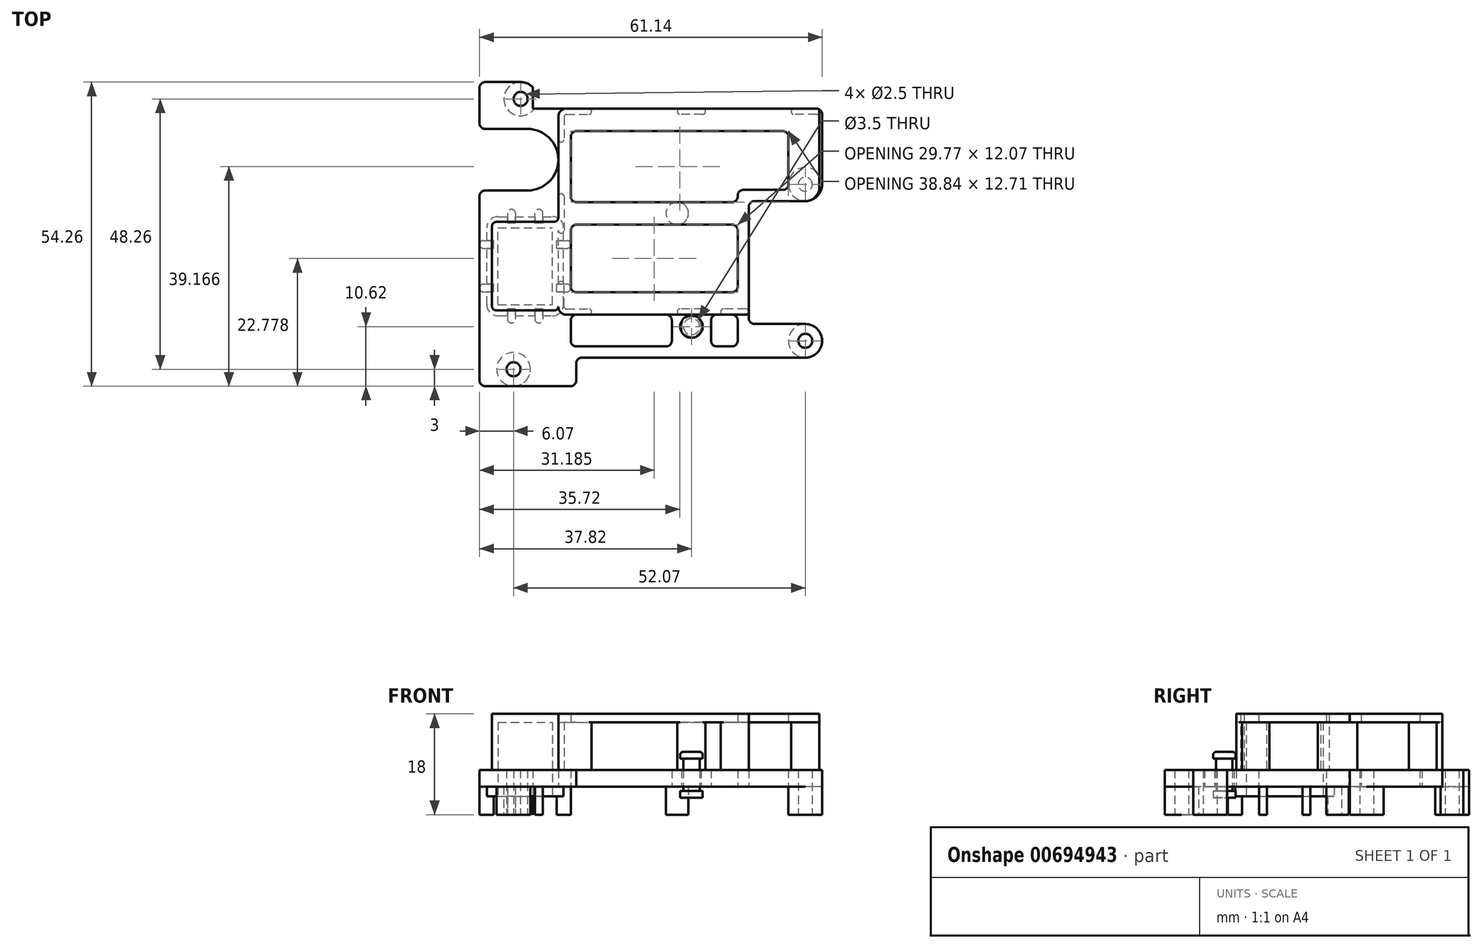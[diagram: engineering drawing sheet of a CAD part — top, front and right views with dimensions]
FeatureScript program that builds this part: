
annotation { "Feature Type Name" : "Feature", "Feature Type Description" : "" }
export const myFeature = defineFeature(function(context is Context, id is Id, definition is map)
    precondition{}
    {
        {
            var Q0;
            Q0=qCreatedBy(makeId("Top.planeOp"),FACE);
            var sketch = newSketch(context, id + "F0", { "sketchPlane" : qUnion([Q0])});
            skCircle(sketch, "E0", {"center": v(0, 0) * mm, "radius": 1.25 * mm});
            skCircle(sketch, "E1", {"center": v(0, 0) * mm, "radius": 3 * mm});
            skCircle(sketch, "E2", {"center": v(1.27, 48.26) * mm, "radius": 2.2 * mm});
            skCircle(sketch, "E3", {"center": v(1.27, 48.26) * mm, "radius": 1.25 * mm});
            skCircle(sketch, "E4", {"center": v(52.07, 33.02) * mm, "radius": 3 * mm});
            skCircle(sketch, "E5", {"center": v(52.07, 33.02) * mm, "radius": 1.25 * mm});
            skCircle(sketch, "E6", {"center": v(52.07, 5.08) * mm, "radius": 3 * mm});
            skCircle(sketch, "E7", {"center": v(52.07, 5.08) * mm, "radius": 1.25 * mm});
            skLineSegment(sketch, "E8.bottom", {"start": v(3.83, 10.75) * mm, "end": v(5.23, 10.75) * mm});
            skLineSegment(sketch, "E8.top", {"start": v(3.83, 8.25) * mm, "end": v(5.23, 8.25) * mm});
            skLineSegment(sketch, "E8.left", {"start": v(3.83, 10.75) * mm, "end": v(3.83, 8.25) * mm});
            skLineSegment(sketch, "E8.right", {"start": v(5.23, 10.75) * mm, "end": v(5.23, 8.25) * mm});
            skLineSegment(sketch, "E9.bottom", {"start": v(3.83, 26.05) * mm, "end": v(5.23, 26.05) * mm});
            skLineSegment(sketch, "E9.top", {"start": v(3.83, 28.55) * mm, "end": v(5.23, 28.55) * mm});
            skLineSegment(sketch, "E9.left", {"start": v(3.83, 26.05) * mm, "end": v(3.83, 28.55) * mm});
            skLineSegment(sketch, "E9.right", {"start": v(5.23, 26.05) * mm, "end": v(5.23, 28.55) * mm});
            skLineSegment(sketch, "E10.bottom", {"start": v(-6.07, 15.2) * mm, "end": v(-3.57, 15.2) * mm});
            skLineSegment(sketch, "E10.top", {"start": v(-6.07, 13.8) * mm, "end": v(-3.57, 13.8) * mm});
            skLineSegment(sketch, "E10.left", {"start": v(-6.07, 15.21) * mm, "end": v(-6.07, 13.8) * mm});
            skLineSegment(sketch, "E10.right", {"start": v(-3.57, 15.2) * mm, "end": v(-3.57, 13.8) * mm});
            skLineSegment(sketch, "E11.bottom", {"start": v(-6.07, 22.99) * mm, "end": v(-3.57, 22.99) * mm});
            skLineSegment(sketch, "E11.top", {"start": v(-6.07, 21.59) * mm, "end": v(-3.57, 21.59) * mm});
            skLineSegment(sketch, "E11.left", {"start": v(-6.07, 23) * mm, "end": v(-6.07, 21.59) * mm});
            skLineSegment(sketch, "E11.right", {"start": v(-3.57, 22.99) * mm, "end": v(-3.57, 21.59) * mm});
            skLineSegment(sketch, "E12.bottom", {"start": v(7.73, 23) * mm, "end": v(10.23, 23) * mm});
            skLineSegment(sketch, "E12.top", {"start": v(7.73, 21.6) * mm, "end": v(10.23, 21.6) * mm});
            skLineSegment(sketch, "E12.left", {"start": v(7.73, 23) * mm, "end": v(7.73, 21.6) * mm});
            skLineSegment(sketch, "E12.right", {"start": v(10.23, 23) * mm, "end": v(10.23, 21.6) * mm});
            skLineSegment(sketch, "E13.bottom", {"start": v(7.73, 15.21) * mm, "end": v(10.23, 15.21) * mm});
            skLineSegment(sketch, "E13.top", {"start": v(7.73, 13.8) * mm, "end": v(10.23, 13.8) * mm});
            skLineSegment(sketch, "E13.left", {"start": v(7.73, 15.21) * mm, "end": v(7.73, 13.81) * mm});
            skLineSegment(sketch, "E13.right", {"start": v(10.23, 15.21) * mm, "end": v(10.23, 13.8) * mm});
            skLineSegment(sketch, "E14.bottom", {"start": v(-1.07, 10.75) * mm, "end": v(0.33, 10.75) * mm});
            skLineSegment(sketch, "E14.top", {"start": v(-1.07, 8.25) * mm, "end": v(0.33, 8.25) * mm});
            skLineSegment(sketch, "E14.left", {"start": v(-1.07, 10.75) * mm, "end": v(-1.07, 8.25) * mm});
            skLineSegment(sketch, "E14.right", {"start": v(0.33, 10.75) * mm, "end": v(0.33, 8.25) * mm});
            skLineSegment(sketch, "E15.bottom", {"start": v(-1.07, 28.55) * mm, "end": v(0.33, 28.55) * mm});
            skLineSegment(sketch, "E15.top", {"start": v(-1.07, 26.05) * mm, "end": v(0.33, 26.05) * mm});
            skLineSegment(sketch, "E15.left", {"start": v(-1.07, 28.55) * mm, "end": v(-1.07, 26.05) * mm});
            skLineSegment(sketch, "E15.right", {"start": v(0.33, 28.55) * mm, "end": v(0.33, 26.05) * mm});
            skCircle(sketch, "E16", {"center": v(29.2, 27.81) * mm, "radius": 2 * mm});
            skArc(sketch, "E17", {"start": v(3.47, 50.3) * mm, "mid": v(-1.73, 48.26) * mm, "end": v(3.47, 46.22) * mm});
            skLineSegment(sketch, "E18", {"start": v(3.47, 50.3) * mm, "end": v(3.47, 46.22) * mm});
            skSolve(sketch);
        }
        {
            var Q0;
            Q0=qCreatedBy(makeId("Top.planeOp"),FACE);
            cPlane(context, id + "F1", {"entities" : qUnion([Q0]), "cplaneType" : CPlaneType.OFFSET, "offset" : 3.3 * mm, "width" : 150 * mm, "height" : 150 * mm});
        }
        {
            var Q0;
            Q0=qCreatedBy(id+"F1.planeOp",FACE);
            var sketch = newSketch(context, id + "F2", { "sketchPlane" : qUnion([Q0])});
            skLineSegment(sketch, "E19.bottom", {"start": v(-2.77, 9.55) * mm, "end": v(6.93, 9.55) * mm});
            skLineSegment(sketch, "E19.top", {"start": v(-2.77, 27.25) * mm, "end": v(6.93, 27.25) * mm});
            skLineSegment(sketch, "E19.left", {"start": v(-4.77, 11.55) * mm, "end": v(-4.77, 25.25) * mm});
            skLineSegment(sketch, "E19.right", {"start": v(8.93, 11.55) * mm, "end": v(8.93, 25.25) * mm});
            skLineSegment(sketch, "E20.bottom", {"start": v(-2.77, 11.55) * mm, "end": v(6.93, 11.55) * mm});
            skLineSegment(sketch, "E20.top", {"start": v(-2.77, 25.25) * mm, "end": v(6.93, 25.25) * mm});
            skLineSegment(sketch, "E20.left", {"start": v(-2.77, 11.55) * mm, "end": v(-2.77, 25.25) * mm});
            skLineSegment(sketch, "E20.right", {"start": v(6.93, 11.55) * mm, "end": v(6.93, 25.25) * mm});
            skArc(sketch, "E21", {"start": v(-4.77, 25.25) * mm, "mid": v(-4.18, 26.66) * mm, "end": v(-2.77, 27.25) * mm});
            skArc(sketch, "E22", {"start": v(6.93, 27.25) * mm, "mid": v(8.34, 26.66) * mm, "end": v(8.93, 25.25) * mm});
            skArc(sketch, "E23", {"start": v(8.93, 11.55) * mm, "mid": v(8.34, 10.14) * mm, "end": v(6.93, 9.55) * mm});
            skArc(sketch, "E24", {"start": v(-2.77, 9.55) * mm, "mid": v(-4.18, 10.14) * mm, "end": v(-4.77, 11.55) * mm});
            skSolve(sketch);
        }
        {
            var Q0;
            Q0=makeQuery(id+"F2.imprint","IMPRINT",FACE,{"disambiguationData":[TD([[makeQuery(id+"F2.imprint","IMPRINT",EDGE,{"derivedFrom":sQuery(id+"F2.wireOp",EDGE,"E19.bottom")}),1.0]])]});
            extrude(context, id + "F3", {"entities" : qUnion([Q0]), "depth" : 1.7 * mm, "offsetDistance" : 25 * mm});
        }
        {
            var Q0;
            Q0=qCreatedBy(makeId("Top.planeOp"),FACE);
            cPlane(context, id + "F4", {"entities" : qUnion([Q0]), "cplaneType" : CPlaneType.OFFSET, "offset" : 5 * mm, "width" : 150 * mm, "height" : 150 * mm});
        }
        {
            var Q0;
            Q0=qCreatedBy(id+"F4.planeOp",FACE);
            var sketch = newSketch(context, id + "F5", { "sketchPlane" : qUnion([Q0])});
            skLineSegment(sketch, "E25", {"start": v(-5.07, -3) * mm, "end": v(10.2, -3) * mm});
            skArc(sketch, "E26", {"start": v(10.2, -3) * mm, "mid": v(10.9, -2.7) * mm, "end": v(11.2, -2) * mm});
            skLineSegment(sketch, "E27", {"start": v(11.2, -2) * mm, "end": v(11.2, 1.08) * mm});
            skArc(sketch, "E28", {"start": v(11.2, 1.08) * mm, "mid": v(11.5, 1.79) * mm, "end": v(12.2, 2.08) * mm});
            skLineSegment(sketch, "E29", {"start": v(12.2, 2.08) * mm, "end": v(52.07, 2.08) * mm});
            skArc(sketch, "E30", {"start": v(52.07, 8.08) * mm, "mid": v(55.07, 5.08) * mm, "end": v(52.07, 2.08) * mm});
            skArc(sketch, "E31", {"start": v(43, 8.08) * mm, "mid": v(42.3, 8.37) * mm, "end": v(42, 9.08) * mm});
            skArc(sketch, "E32", {"start": v(42, 29.02) * mm, "mid": v(42.3, 29.73) * mm, "end": v(43, 30.02) * mm});
            skArc(sketch, "E33", {"start": v(55.07, 33.02) * mm, "mid": v(54.2, 30.9) * mm, "end": v(52.07, 30.02) * mm});
            skLineSegment(sketch, "E34", {"start": v(52.07, 8.08) * mm, "end": v(43, 8.08) * mm});
            skLineSegment(sketch, "E35", {"start": v(52.07, 30.02) * mm, "end": v(43, 30.02) * mm});
            skLineSegment(sketch, "E36", {"start": v(42, 9.08) * mm, "end": v(42, 29.02) * mm});
            skLineSegment(sketch, "E37", {"start": v(55.07, 33.02) * mm, "end": v(55.07, 45.52) * mm});
            skArc(sketch, "E38", {"start": v(55.07, 45.52) * mm, "mid": v(54.78, 46.23) * mm, "end": v(54.07, 46.52) * mm});
            skLineSegment(sketch, "E39", {"start": v(54.07, 46.52) * mm, "end": v(3.62, 46.52) * mm});
            skArc(sketch, "E40", {"start": v(3.62, 46.52) * mm, "mid": v(3.51, 46.56) * mm, "end": v(3.47, 46.67) * mm});
            skLineSegment(sketch, "E41", {"start": v(3.47, 46.67) * mm, "end": v(3.47, 50.3) * mm});
            skArc(sketch, "E42", {"start": v(3.47, 50.3) * mm, "mid": v(2.47, 51) * mm, "end": v(1.27, 51.26) * mm});
            skLineSegment(sketch, "E43", {"start": v(1.27, 51.26) * mm, "end": v(-5.07, 51.26) * mm});
            skArc(sketch, "E44", {"start": v(-5.07, 51.26) * mm, "mid": v(-5.78, 50.97) * mm, "end": v(-6.07, 50.26) * mm});
            skArc(sketch, "E45", {"start": v(-6.07, 43.9) * mm, "mid": v(-5.78, 43.2) * mm, "end": v(-5.07, 42.9) * mm});
            skArc(sketch, "E46", {"start": v(2.49, 42.9) * mm, "mid": v(7.99, 37.4) * mm, "end": v(2.49, 31.9) * mm});
            skArc(sketch, "E47", {"start": v(-6.07, 30.9) * mm, "mid": v(-5.78, 31.6) * mm, "end": v(-5.07, 31.9) * mm});
            skLineSegment(sketch, "E48", {"start": v(-5.07, 31.9) * mm, "end": v(2.49, 31.9) * mm});
            skLineSegment(sketch, "E49", {"start": v(2.49, 42.9) * mm, "end": v(-5.07, 42.9) * mm});
            skLineSegment(sketch, "E50", {"start": v(-6.07, 43.9) * mm, "end": v(-6.07, 50.26) * mm});
            skLineSegment(sketch, "E51.bottom", {"start": v(-2.77, 11.55) * mm, "end": v(6.93, 11.55) * mm});
            skLineSegment(sketch, "E51.top", {"start": v(-2.77, 25.25) * mm, "end": v(6.93, 25.25) * mm});
            skLineSegment(sketch, "E51.left", {"start": v(-2.77, 11.55) * mm, "end": v(-2.77, 25.25) * mm});
            skLineSegment(sketch, "E51.right", {"start": v(6.93, 11.55) * mm, "end": v(6.93, 25.25) * mm});
            skLineSegment(sketch, "E52", {"start": v(-6.07, 30.9) * mm, "end": v(-6.07, -2) * mm});
            skArc(sketch, "E53", {"start": v(-6.07, -2) * mm, "mid": v(-5.78, -2.7) * mm, "end": v(-5.07, -3) * mm});
            skArc(sketch, "E54", {"start": v(10.23, 41.52) * mm, "mid": v(10.52, 42.23) * mm, "end": v(11.23, 42.52) * mm});
            skArc(sketch, "E55", {"start": v(49.07, 41.52) * mm, "mid": v(48.78, 42.23) * mm, "end": v(48.07, 42.52) * mm});
            skArc(sketch, "E56", {"start": v(48.07, 32.02) * mm, "mid": v(48.78, 32.31) * mm, "end": v(49.07, 33.02) * mm});
            skArc(sketch, "E57", {"start": v(40, 31.02) * mm, "mid": v(40.3, 31.73) * mm, "end": v(41, 32.02) * mm});
            skArc(sketch, "E58", {"start": v(40, 5.08) * mm, "mid": v(39.7, 4.37) * mm, "end": v(39, 4.08) * mm});
            skArc(sketch, "E59", {"start": v(10.23, 5.08) * mm, "mid": v(10.52, 4.37) * mm, "end": v(11.23, 4.08) * mm});
            skLineSegment(sketch, "E60", {"start": v(11.23, 42.52) * mm, "end": v(48.07, 42.52) * mm});
            skLineSegment(sketch, "E61", {"start": v(49.07, 41.52) * mm, "end": v(49.07, 33.02) * mm});
            skLineSegment(sketch, "E62", {"start": v(48.07, 32.02) * mm, "end": v(41, 32.02) * mm});
            skLineSegment(sketch, "E63", {"start": v(39, 4.08) * mm, "end": v(11.23, 4.08) * mm});
            skLineSegment(sketch, "E64", {"start": v(11.23, 25.81) * mm, "end": v(39, 25.81) * mm});
            skLineSegment(sketch, "E65", {"start": v(11.23, 29.81) * mm, "end": v(39, 29.81) * mm});
            skArc(sketch, "E66", {"start": v(40, 24.81) * mm, "mid": v(39.7, 25.52) * mm, "end": v(39, 25.81) * mm});
            skArc(sketch, "E67", {"start": v(11.23, 25.81) * mm, "mid": v(10.52, 25.52) * mm, "end": v(10.23, 24.81) * mm});
            skArc(sketch, "E68", {"start": v(10.23, 30.81) * mm, "mid": v(10.52, 30.1) * mm, "end": v(11.23, 29.81) * mm});
            skArc(sketch, "E69", {"start": v(39, 29.81) * mm, "mid": v(39.7, 30.1) * mm, "end": v(40, 30.81) * mm});
            skLineSegment(sketch, "E70", {"start": v(10.23, 30.81) * mm, "end": v(10.23, 41.52) * mm});
            skLineSegment(sketch, "E71", {"start": v(40, 31.02) * mm, "end": v(40, 30.81) * mm});
            skArc(sketch, "E72", {"start": v(10.23, 8.74) * mm, "mid": v(10.52, 9.45) * mm, "end": v(11.23, 9.74) * mm});
            skArc(sketch, "E73", {"start": v(10.23, 14.74) * mm, "mid": v(10.52, 14.04) * mm, "end": v(11.23, 13.74) * mm});
            skArc(sketch, "E74", {"start": v(40, 14.74) * mm, "mid": v(39.7, 14.04) * mm, "end": v(39, 13.74) * mm});
            skArc(sketch, "E75", {"start": v(39, 9.74) * mm, "mid": v(39.7, 9.45) * mm, "end": v(40, 8.74) * mm});
            skLineSegment(sketch, "E76", {"start": v(11.23, 9.74) * mm, "end": v(39, 9.74) * mm});
            skLineSegment(sketch, "E77", {"start": v(11.23, 13.74) * mm, "end": v(39, 13.74) * mm});
            skLineSegment(sketch, "E78", {"start": v(40, 14.74) * mm, "end": v(40, 24.81) * mm});
            skLineSegment(sketch, "E79", {"start": v(10.23, 14.74) * mm, "end": v(10.23, 24.81) * mm});
            skLineSegment(sketch, "E80", {"start": v(40, 8.74) * mm, "end": v(40, 5.08) * mm});
            skLineSegment(sketch, "E81", {"start": v(10.23, 8.74) * mm, "end": v(10.23, 5.08) * mm});
            skCircle(sketch, "E82", {"center": v(0, 0) * mm, "radius": 1.25 * mm});
            skCircle(sketch, "E83", {"center": v(52.07, 5.08) * mm, "radius": 1.25 * mm});
            skCircle(sketch, "E84", {"center": v(52.07, 33.02) * mm, "radius": 1.25 * mm});
            skCircle(sketch, "E85", {"center": v(1.27, 48.26) * mm, "radius": 1.25 * mm});
            skCircle(sketch, "E86", {"center": v(31.75, 7.62) * mm, "radius": 1.75 * mm});
            skArc(sketch, "E87", {"start": v(27.25, 9.74) * mm, "mid": v(27.96, 9.45) * mm, "end": v(28.25, 8.74) * mm});
            skArc(sketch, "E88", {"start": v(27.25, 4.08) * mm, "mid": v(27.96, 4.37) * mm, "end": v(28.25, 5.08) * mm});
            skArc(sketch, "E89", {"start": v(36.25, 4.08) * mm, "mid": v(35.54, 4.37) * mm, "end": v(35.25, 5.08) * mm});
            skArc(sketch, "E90", {"start": v(36.25, 9.74) * mm, "mid": v(35.54, 9.45) * mm, "end": v(35.25, 8.74) * mm});
            skLineSegment(sketch, "E91", {"start": v(31.75, 8.52) * mm, "end": v(31.75, 6.64) * mm});
            skLineSegment(sketch, "E92", {"start": v(28.25, 5.08) * mm, "end": v(28.25, 8.74) * mm});
            skLineSegment(sketch, "E93", {"start": v(35.25, 8.74) * mm, "end": v(35.25, 5.08) * mm});
            skSolve(sketch);
        }
        {
            var Q0;
            Q0=makeQuery(id+"F5.imprint","IMPRINT",FACE,{"disambiguationData":[TD([[makeQuery(id+"F5.imprint","IMPRINT",EDGE,{"derivedFrom":sQuery(id+"F5.wireOp",EDGE,"E25")}),1.0]])]});
            var Q1;
            Q1=makeQuery(id+"F5.imprint","IMPRINT",FACE,{"disambiguationData":[TD([[makeQuery(id+"F5.imprint","IMPRINT",EDGE,{"derivedFrom":sQuery(id+"F5.wireOp",EDGE,"E86")}),-1.0]])]});
            extrude(context, id + "F6", {"entities" : qUnion([Q0, Q1]), "operationType" : NewBodyOperationType.ADD, "depth" : 3 * mm, "offsetDistance" : 25 * mm});
        }
        {
            var Q0;
            Q0=makeQuery(id+"F0.imprint","IMPRINT",FACE,{"disambiguationData":[TD([[makeQuery(id+"F0.imprint","IMPRINT",EDGE,{"derivedFrom":sQuery(id+"F0.wireOp",EDGE,"E0")}),-1.0]])]});
            var Q1;
            Q1=makeQuery(id+"F0.imprint","IMPRINT",FACE,{"disambiguationData":[TD([[makeQuery(id+"F0.imprint","IMPRINT",EDGE,{"derivedFrom":sQuery(id+"F0.wireOp",EDGE,"E2")}),1.0]])]});
            var Q2;
            Q2=makeQuery(id+"F0.imprint","IMPRINT",FACE,{"disambiguationData":[TD([[makeQuery(id+"F0.imprint","IMPRINT",EDGE,{"derivedFrom":sQuery(id+"F0.wireOp",EDGE,"E4")}),1.0]])]});
            var Q3;
            Q3=makeQuery(id+"F0.imprint","IMPRINT",FACE,{"disambiguationData":[TD([[makeQuery(id+"F0.imprint","IMPRINT",EDGE,{"derivedFrom":sQuery(id+"F0.wireOp",EDGE,"E6")}),1.0]])]});
            var Q4;
            {var subQ0=sQuery(id+"F0.wireOp",EDGE,"E2");Q4=makeQuery(id+"F0.imprint","IMPRINT",FACE,{"disambiguationData":[TD([[makeQuery(id+"F0.imprint","IMPRINT",EDGE,{"derivedFrom":subQ0}),-1.0]])]});}
            extrude(context, id + "F7", {"entities" : qUnion([Q0, Q1, Q2, Q3, Q4]), "operationType" : NewBodyOperationType.ADD, "depth" : 5 * mm, "offsetDistance" : 25 * mm});
        }
        {
            var Q0;
            Q0=makeQuery(id+"F0.imprint","IMPRINT",FACE,{"disambiguationData":[TD([[makeQuery(id+"F0.imprint","IMPRINT",EDGE,{"derivedFrom":sQuery(id+"F0.wireOp",EDGE,"E16")}),1.0]])]});
            var Q1;
            Q1=makeQuery(id+"F0.imprint","IMPRINT",FACE,{"disambiguationData":[TD([[makeQuery(id+"F0.imprint","IMPRINT",EDGE,{"derivedFrom":sQuery(id+"F0.wireOp",EDGE,"E15.bottom")}),-1.0]])]});
            var Q2;
            Q2=makeQuery(id+"F0.imprint","IMPRINT",FACE,{"disambiguationData":[TD([[makeQuery(id+"F0.imprint","IMPRINT",EDGE,{"derivedFrom":sQuery(id+"F0.wireOp",EDGE,"E9.bottom")}),1.0]])]});
            var Q3;
            Q3=makeQuery(id+"F0.imprint","IMPRINT",FACE,{"disambiguationData":[TD([[makeQuery(id+"F0.imprint","IMPRINT",EDGE,{"derivedFrom":sQuery(id+"F0.wireOp",EDGE,"E12.bottom")}),-1.0]])]});
            var Q4;
            Q4=makeQuery(id+"F0.imprint","IMPRINT",FACE,{"disambiguationData":[TD([[makeQuery(id+"F0.imprint","IMPRINT",EDGE,{"derivedFrom":sQuery(id+"F0.wireOp",EDGE,"E13.bottom")}),-1.0]])]});
            var Q5;
            Q5=makeQuery(id+"F0.imprint","IMPRINT",FACE,{"disambiguationData":[TD([[makeQuery(id+"F0.imprint","IMPRINT",EDGE,{"derivedFrom":sQuery(id+"F0.wireOp",EDGE,"E8.bottom")}),-1.0]])]});
            var Q6;
            Q6=makeQuery(id+"F0.imprint","IMPRINT",FACE,{"disambiguationData":[TD([[makeQuery(id+"F0.imprint","IMPRINT",EDGE,{"derivedFrom":sQuery(id+"F0.wireOp",EDGE,"E14.bottom")}),-1.0]])]});
            var Q7;
            Q7=makeQuery(id+"F0.imprint","IMPRINT",FACE,{"disambiguationData":[TD([[makeQuery(id+"F0.imprint","IMPRINT",EDGE,{"derivedFrom":sQuery(id+"F0.wireOp",EDGE,"E10.bottom")}),-1.0]])]});
            var Q8;
            Q8=makeQuery(id+"F0.imprint","IMPRINT",FACE,{"disambiguationData":[TD([[makeQuery(id+"F0.imprint","IMPRINT",EDGE,{"derivedFrom":sQuery(id+"F0.wireOp",EDGE,"E11.bottom")}),-1.0]])]});
            extrude(context, id + "F8", {"entities" : qUnion([Q0, Q1, Q2, Q3, Q4, Q5, Q6, Q7, Q8]), "operationType" : NewBodyOperationType.ADD, "depth" : 5 * mm, "offsetDistance" : 25 * mm});
        }
        {
            var Q0;
            Q0=qCreatedBy(makeId("Top.planeOp"),FACE);
            cPlane(context, id + "F9", {"entities" : qUnion([Q0]), "cplaneType" : CPlaneType.OFFSET, "offset" : 8 * mm, "width" : 150 * mm, "height" : 150 * mm});
        }
        {
            var Q0;
            Q0=qCreatedBy(id+"F9.planeOp",FACE);
            var sketch = newSketch(context, id + "F10", { "sketchPlane" : qUnion([Q0])});
            skArc(sketch, "E94", {"start": v(41.48, 9.74) * mm, "mid": v(42, 10.26) * mm, "end": v(41.48, 10.78) * mm});
            skArc(sketch, "E95", {"start": v(54.07, 45.48) * mm, "mid": v(54.59, 46) * mm, "end": v(54.07, 46.52) * mm});
            skLineSegment(sketch, "E96", {"start": v(9.41, 46.52) * mm, "end": v(13.41, 46.52) * mm});
            skLineSegment(sketch, "E97", {"start": v(9.41, 9.74) * mm, "end": v(13.41, 9.74) * mm});
            skLineSegment(sketch, "E98", {"start": v(7.99, 11.17) * mm, "end": v(7.99, 15.17) * mm});
            skLineSegment(sketch, "E99", {"start": v(7.99, 45.1) * mm, "end": v(7.99, 41.1) * mm});
            skLineSegment(sketch, "E100", {"start": v(54.07, 46.52) * mm, "end": v(50.07, 46.52) * mm});
            skLineSegment(sketch, "E101", {"start": v(41.48, 9.74) * mm, "end": v(37.48, 9.74) * mm});
            skLineSegment(sketch, "E102", {"start": v(54.07, 45.48) * mm, "end": v(50.07, 45.48) * mm});
            skLineSegment(sketch, "E103", {"start": v(41.48, 10.78) * mm, "end": v(37.48, 10.78) * mm});
            skArc(sketch, "E104", {"start": v(13.41, 45.48) * mm, "mid": v(13.93, 46) * mm, "end": v(13.41, 46.52) * mm});
            skArc(sketch, "E105", {"start": v(37.48, 10.78) * mm, "mid": v(36.96, 10.26) * mm, "end": v(37.48, 9.74) * mm});
            skArc(sketch, "E106", {"start": v(13.41, 9.74) * mm, "mid": v(13.93, 10.26) * mm, "end": v(13.41, 10.78) * mm});
            skArc(sketch, "E107", {"start": v(9.03, 15.17) * mm, "mid": v(8.5, 15.69) * mm, "end": v(7.99, 15.17) * mm});
            skArc(sketch, "E108", {"start": v(7.99, 41.1) * mm, "mid": v(8.5, 40.58) * mm, "end": v(9.03, 41.1) * mm});
            skArc(sketch, "E109", {"start": v(50.07, 46.52) * mm, "mid": v(49.55, 46) * mm, "end": v(50.07, 45.48) * mm});
            skLineSegment(sketch, "E110", {"start": v(9.03, 11.17) * mm, "end": v(9.03, 15.17) * mm});
            skLineSegment(sketch, "E111", {"start": v(9.03, 45.1) * mm, "end": v(9.03, 41.1) * mm});
            skLineSegment(sketch, "E112", {"start": v(9.41, 45.48) * mm, "end": v(13.41, 45.48) * mm});
            skArc(sketch, "E113", {"start": v(9.41, 45.48) * mm, "mid": v(9.14, 45.37) * mm, "end": v(9.03, 45.1) * mm});
            skArc(sketch, "E114", {"start": v(9.03, 11.17) * mm, "mid": v(9.14, 10.9) * mm, "end": v(9.41, 10.78) * mm});
            skLineSegment(sketch, "E115", {"start": v(9.41, 10.78) * mm, "end": v(13.41, 10.78) * mm});
            skArc(sketch, "E116", {"start": v(7.99, 11.17) * mm, "mid": v(8.4, 10.16) * mm, "end": v(9.41, 9.74) * mm});
            skArc(sketch, "E117", {"start": v(9.41, 46.52) * mm, "mid": v(8.4, 46.1) * mm, "end": v(7.99, 45.1) * mm});
            skArc(sketch, "E118", {"start": v(33.74, 9.74) * mm, "mid": v(34.26, 10.26) * mm, "end": v(33.74, 10.78) * mm});
            skLineSegment(sketch, "E119", {"start": v(33.74, 9.74) * mm, "end": v(29.74, 9.74) * mm});
            skLineSegment(sketch, "E120", {"start": v(33.74, 10.78) * mm, "end": v(29.74, 10.78) * mm});
            skArc(sketch, "E121", {"start": v(29.74, 10.78) * mm, "mid": v(29.22, 10.26) * mm, "end": v(29.74, 9.74) * mm});
            skArc(sketch, "E122", {"start": v(33.74, 45.48) * mm, "mid": v(34.26, 46) * mm, "end": v(33.74, 46.52) * mm});
            skLineSegment(sketch, "E123", {"start": v(33.74, 45.48) * mm, "end": v(29.74, 45.48) * mm});
            skLineSegment(sketch, "E124", {"start": v(33.74, 46.52) * mm, "end": v(29.74, 46.52) * mm});
            skArc(sketch, "E125", {"start": v(29.74, 46.52) * mm, "mid": v(29.22, 46) * mm, "end": v(29.74, 45.48) * mm});
            skArc(sketch, "E126", {"start": v(9.03, 30.81) * mm, "mid": v(8.5, 31.33) * mm, "end": v(7.99, 30.81) * mm});
            skLineSegment(sketch, "E127", {"start": v(9.03, 30.81) * mm, "end": v(9.03, 24.81) * mm});
            skLineSegment(sketch, "E128", {"start": v(7.99, 30.81) * mm, "end": v(7.99, 24.81) * mm});
            skArc(sketch, "E129", {"start": v(7.99, 24.81) * mm, "mid": v(8.5, 24.3) * mm, "end": v(9.03, 24.81) * mm});
            skLineSegment(sketch, "E130", {"start": v(7.99, 15.17) * mm, "end": v(7.99, 26.3) * mm});
            skLineSegment(sketch, "E131", {"start": v(7.99, 26.3) * mm, "end": v(-3.83, 26.3) * mm});
            skLineSegment(sketch, "E132", {"start": v(-3.83, 26.3) * mm, "end": v(-3.83, 10.5) * mm});
            skLineSegment(sketch, "E133", {"start": v(-3.83, 10.5) * mm, "end": v(7.99, 10.5) * mm});
            skLineSegment(sketch, "E134.bottom", {"start": v(-2.77, 25.25) * mm, "end": v(6.93, 25.25) * mm});
            skLineSegment(sketch, "E134.top", {"start": v(-2.77, 11.55) * mm, "end": v(6.93, 11.55) * mm});
            skLineSegment(sketch, "E134.left", {"start": v(-2.77, 25.25) * mm, "end": v(-2.77, 11.55) * mm});
            skLineSegment(sketch, "E134.right", {"start": v(6.93, 25.25) * mm, "end": v(6.93, 11.55) * mm});
            skLineSegment(sketch, "E135", {"start": v(7.99, 11.17) * mm, "end": v(7.99, 10.5) * mm});
            skSolve(sketch);
        }
        {
            var Q0;
            Q0=qCreatedBy(makeId("Top.planeOp"),FACE);
            cPlane(context, id + "F11", {"entities" : qUnion([Q0]), "cplaneType" : CPlaneType.OFFSET, "offset" : 3 * mm, "width" : 150 * mm, "height" : 150 * mm});
        }
        {
            var Q0;
            Q0=qCreatedBy(id+"F11.planeOp",FACE);
            var sketch = newSketch(context, id + "F12", { "sketchPlane" : qUnion([Q0])});
            skCircle(sketch, "E136", {"center": v(31.75, 7.62) * mm, "radius": 2 * mm});
            skCircle(sketch, "E137", {"center": v(31.75, 7.62) * mm, "radius": 1.45 * mm});
            skSolve(sketch);
        }
        {
            var Q0;
            Q0 = qSketchRegion(id + "F12", true);
            extrude(context, id + "F13", {"entities" : qUnion([Q0]), "depth" : 1.2 * mm, "offsetDistance" : 25 * mm});
        }
        {
            var Q0;
            Q0=makeQuery(id+"F12.imprint","IMPRINT",FACE,{"disambiguationData":[TD([[makeQuery(id+"F12.imprint","IMPRINT",EDGE,{"derivedFrom":sQuery(id+"F12.wireOp",EDGE,"E137")}),1.0]])]});
            extrude(context, id + "F14", {"entities" : qUnion([Q0]), "operationType" : NewBodyOperationType.ADD, "depth" : 7 * mm, "offsetDistance" : 25 * mm});
        }
        {
            var Q0;
            Q0=qCreatedBy(id+"F11.planeOp",FACE);
            cPlane(context, id + "F15", {"entities" : qUnion([Q0]), "cplaneType" : CPlaneType.OFFSET, "offset" : 7 * mm, "width" : 150 * mm, "height" : 150 * mm});
        }
        {
            var Q0;
            Q0=qCreatedBy(id+"F15.planeOp",FACE);
            var sketch = newSketch(context, id + "F16", { "sketchPlane" : qUnion([Q0])});
            skCircle(sketch, "E138", {"center": v(31.75, 7.62) * mm, "radius": 2 * mm});
            skSolve(sketch);
        }
        {
            var Q0;
            Q0=makeQuery(id+"F16.imprint","IMPRINT",FACE,{"disambiguationData":[TD([[makeQuery(id+"F16.imprint","IMPRINT",EDGE,{"derivedFrom":sQuery(id+"F16.wireOp",EDGE,"E138")}),1.0]])]});
            extrude(context, id + "F17", {"entities" : qUnion([Q0]), "operationType" : NewBodyOperationType.ADD, "depth" : 1.2 * mm, "offsetDistance" : 25 * mm});
        }
        {
            var Q0;
            Q0 = qSketchRegion(id + "F10", true);
            extrude(context, id + "F18", {"entities" : qUnion([Q0]), "operationType" : NewBodyOperationType.ADD, "depth" : 8.5 * mm, "offsetDistance" : 25 * mm});
        }
        {
            var Q0;
            Q0=qCreatedBy(id+"F9.planeOp",FACE);
            cPlane(context, id + "F19", {"entities" : qUnion([Q0]), "cplaneType" : CPlaneType.OFFSET, "offset" : 8.5 * mm, "width" : 150 * mm, "height" : 150 * mm});
        }
        {
            var Q0;
            Q0=qCreatedBy(id+"F19.planeOp",FACE);
            var sketch = newSketch(context, id + "F20", { "sketchPlane" : qUnion([Q0])});
            skArc(sketch, "E139", {"start": v(7.99, 11.17) * mm, "mid": v(8.4, 10.16) * mm, "end": v(9.41, 9.74) * mm});
            skArc(sketch, "E140", {"start": v(42, 10.26) * mm, "mid": v(41.85, 9.9) * mm, "end": v(41.48, 9.74) * mm});
            skArc(sketch, "E141", {"start": v(43, 30.02) * mm, "mid": v(42.3, 29.73) * mm, "end": v(42, 29.02) * mm});
            skArc(sketch, "E142", {"start": v(54.59, 32.54) * mm, "mid": v(53.85, 30.76) * mm, "end": v(52.07, 30.02) * mm});
            skArc(sketch, "E143", {"start": v(54.59, 46) * mm, "mid": v(54.44, 46.37) * mm, "end": v(54.07, 46.52) * mm});
            skArc(sketch, "E144", {"start": v(9.41, 46.52) * mm, "mid": v(8.4, 46.1) * mm, "end": v(7.99, 45.1) * mm});
            skLineSegment(sketch, "E145", {"start": v(9.41, 46.52) * mm, "end": v(54.07, 46.52) * mm});
            skLineSegment(sketch, "E146", {"start": v(54.59, 46) * mm, "end": v(54.59, 32.54) * mm});
            skLineSegment(sketch, "E147", {"start": v(52.07, 30.02) * mm, "end": v(43, 30.02) * mm});
            skLineSegment(sketch, "E148", {"start": v(42, 29.02) * mm, "end": v(42, 10.26) * mm});
            skLineSegment(sketch, "E149", {"start": v(41.48, 9.74) * mm, "end": v(9.41, 9.74) * mm});
            skLineSegment(sketch, "E150", {"start": v(7.99, 11.17) * mm, "end": v(7.99, 45.1) * mm});
            skArc(sketch, "E151", {"start": v(10.23, 41.52) * mm, "mid": v(10.52, 42.23) * mm, "end": v(11.23, 42.52) * mm});
            skArc(sketch, "E152", {"start": v(49.07, 41.52) * mm, "mid": v(48.78, 42.23) * mm, "end": v(48.07, 42.52) * mm});
            skArc(sketch, "E153", {"start": v(48.07, 32.02) * mm, "mid": v(48.78, 32.31) * mm, "end": v(49.07, 33.02) * mm});
            skArc(sketch, "E154", {"start": v(40, 31.02) * mm, "mid": v(40.3, 31.73) * mm, "end": v(41, 32.02) * mm});
            skLineSegment(sketch, "E155", {"start": v(11.23, 42.52) * mm, "end": v(48.07, 42.52) * mm});
            skLineSegment(sketch, "E156", {"start": v(49.07, 41.52) * mm, "end": v(49.07, 33.02) * mm});
            skLineSegment(sketch, "E157", {"start": v(48.07, 32.02) * mm, "end": v(41, 32.02) * mm});
            skLineSegment(sketch, "E158", {"start": v(11.23, 25.81) * mm, "end": v(39, 25.81) * mm});
            skLineSegment(sketch, "E159", {"start": v(11.23, 29.81) * mm, "end": v(39, 29.81) * mm});
            skArc(sketch, "E160", {"start": v(40, 24.81) * mm, "mid": v(39.7, 25.52) * mm, "end": v(39, 25.81) * mm});
            skArc(sketch, "E161", {"start": v(11.23, 25.81) * mm, "mid": v(10.52, 25.52) * mm, "end": v(10.23, 24.81) * mm});
            skArc(sketch, "E162", {"start": v(10.23, 30.81) * mm, "mid": v(10.52, 30.1) * mm, "end": v(11.23, 29.81) * mm});
            skArc(sketch, "E163", {"start": v(39, 29.81) * mm, "mid": v(39.7, 30.1) * mm, "end": v(40, 30.81) * mm});
            skLineSegment(sketch, "E164", {"start": v(10.23, 30.81) * mm, "end": v(10.23, 41.52) * mm});
            skLineSegment(sketch, "E165", {"start": v(40, 31.02) * mm, "end": v(40, 30.81) * mm});
            skArc(sketch, "E166", {"start": v(10.23, 14.74) * mm, "mid": v(10.52, 14.04) * mm, "end": v(11.23, 13.74) * mm});
            skArc(sketch, "E167", {"start": v(40, 14.74) * mm, "mid": v(39.7, 14.04) * mm, "end": v(39, 13.74) * mm});
            skLineSegment(sketch, "E168", {"start": v(11.23, 13.74) * mm, "end": v(39, 13.74) * mm});
            skLineSegment(sketch, "E169", {"start": v(40, 14.74) * mm, "end": v(40, 24.81) * mm});
            skLineSegment(sketch, "E170", {"start": v(10.23, 14.74) * mm, "end": v(10.23, 24.81) * mm});
            skLineSegment(sketch, "E171.bottom", {"start": v(-3.83, 26.3) * mm, "end": v(7.99, 26.3) * mm});
            skLineSegment(sketch, "E171.top", {"start": v(-3.83, 10.5) * mm, "end": v(7.99, 10.5) * mm});
            skLineSegment(sketch, "E171.left", {"start": v(-3.83, 26.3) * mm, "end": v(-3.83, 10.5) * mm});
            skLineSegment(sketch, "E171.right", {"start": v(7.99, 26.3) * mm, "end": v(7.99, 10.5) * mm});
            skSolve(sketch);
        }
        {
            var Q0;
            Q0 = qSketchRegion(id + "F20", true);
            extrude(context, id + "F21", {"entities" : qUnion([Q0]), "operationType" : NewBodyOperationType.ADD, "depth" : 1.5 * mm, "offsetDistance" : 25 * mm});
        }
        {
            var Q0;
            Q0=makeQuery(id+"F21.boolean.opBoolean","MERGE",EDGE,{"derivedFrom":[makeQuery(id+"F18.opExtrude","SWEPT_EDGE",EDGE,{"disambiguationData":[OSD([sQuery(id+"F10.wireOp",EDGE,"E131"),sQuery(id+"F10.wireOp",EDGE,"E132")])]}),makeQuery(id+"F21.opExtrude","SWEPT_EDGE",EDGE,{"disambiguationData":[OSD([sQuery(id+"F20.wireOp",EDGE,"E171.bottom"),sQuery(id+"F20.wireOp",EDGE,"E171.left")])]})]});
            var Q1;
            Q1=makeQuery(id+"F21.boolean.opBoolean","MERGE",EDGE,{"derivedFrom":[makeQuery(id+"F18.opExtrude","SWEPT_EDGE",EDGE,{"disambiguationData":[OSD([sQuery(id+"F10.wireOp",EDGE,"E132"),sQuery(id+"F10.wireOp",EDGE,"E133")])]}),makeQuery(id+"F21.opExtrude","SWEPT_EDGE",EDGE,{"disambiguationData":[OSD([sQuery(id+"F20.wireOp",EDGE,"E171.top"),sQuery(id+"F20.wireOp",EDGE,"E171.left")])]})]});
            var Q2;
            Q2=makeQuery(id+"F21.boolean.opBoolean","MERGE",EDGE,{"derivedFrom":[makeQuery(id+"F18.opExtrude","SWEPT_EDGE",EDGE,{"disambiguationData":[OSD([sQuery(id+"F10.wireOp",EDGE,"E128"),sQuery(id+"F10.wireOp",EDGE,"E130"),sQuery(id+"F10.wireOp",EDGE,"E131")])]}),makeQuery(id+"F21.opExtrude","SWEPT_EDGE",EDGE,{"disambiguationData":[OSD([sQuery(id+"F20.wireOp",EDGE,"E150"),sQuery(id+"F20.wireOp",EDGE,"E171.bottom"),sQuery(id+"F20.wireOp",EDGE,"E171.right")])]})]});
            var Q3;
            Q3=makeQuery(id+"F21.boolean.opBoolean","MERGE",EDGE,{"derivedFrom":[makeQuery(id+"F18.opExtrude","SWEPT_EDGE",EDGE,{"disambiguationData":[OSD([sQuery(id+"F10.wireOp",EDGE,"E133"),sQuery(id+"F10.wireOp",EDGE,"E135")])]}),makeQuery(id+"F21.opExtrude","SWEPT_EDGE",EDGE,{"disambiguationData":[OSD([sQuery(id+"F20.wireOp",EDGE,"E171.top"),sQuery(id+"F20.wireOp",EDGE,"E171.right")])]})]});
            fillet(context, id + "F22", {"entities" : qUnion([Q0, Q1, Q2, Q3]), "radius" : 0.75 * mm, "tangentPropagation" : true, "allowEdgeOverflow" : false});
        }
        {
            var Q0;
            Q0=makeQuery(id+"F17.opExtrude","CAP_EDGE",EDGE,{"disambiguationData":[OSD([sQuery(id+"F16.wireOp",EDGE,"E138")])],"isStart":false});
            fillet(context, id + "F23", {"entities" : qUnion([Q0]), "radius" : 0.5 * mm, "tangentPropagation" : true, "allowEdgeOverflow" : false});
        }
        {
            var Q0;
            Q0=makeQuery(id+"F8.opExtrude","SWEPT_EDGE",EDGE,{"disambiguationData":[OSD([sQuery(id+"F0.wireOp",EDGE,"E12.bottom"),sQuery(id+"F0.wireOp",EDGE,"E12.right")])]});
            var Q1;
            Q1=makeQuery(id+"F8.opExtrude","SWEPT_EDGE",EDGE,{"disambiguationData":[OSD([sQuery(id+"F0.wireOp",EDGE,"E12.top"),sQuery(id+"F0.wireOp",EDGE,"E12.right")])]});
            var Q2;
            Q2=makeQuery(id+"F8.opExtrude","SWEPT_EDGE",EDGE,{"disambiguationData":[OSD([sQuery(id+"F0.wireOp",EDGE,"E13.bottom"),sQuery(id+"F0.wireOp",EDGE,"E13.right")])]});
            var Q3;
            Q3=makeQuery(id+"F8.opExtrude","SWEPT_EDGE",EDGE,{"disambiguationData":[OSD([sQuery(id+"F0.wireOp",EDGE,"E13.top"),sQuery(id+"F0.wireOp",EDGE,"E13.right")])]});
            var Q4;
            Q4=makeQuery(id+"F8.opExtrude","SWEPT_EDGE",EDGE,{"disambiguationData":[OSD([sQuery(id+"F0.wireOp",EDGE,"E8.top"),sQuery(id+"F0.wireOp",EDGE,"E8.right")])]});
            var Q5;
            Q5=makeQuery(id+"F8.opExtrude","SWEPT_EDGE",EDGE,{"disambiguationData":[OSD([sQuery(id+"F0.wireOp",EDGE,"E8.top"),sQuery(id+"F0.wireOp",EDGE,"E8.left")])]});
            var Q6;
            Q6=makeQuery(id+"F8.opExtrude","SWEPT_EDGE",EDGE,{"disambiguationData":[OSD([sQuery(id+"F0.wireOp",EDGE,"E14.top"),sQuery(id+"F0.wireOp",EDGE,"E14.right")])]});
            var Q7;
            Q7=makeQuery(id+"F8.opExtrude","SWEPT_EDGE",EDGE,{"disambiguationData":[OSD([sQuery(id+"F0.wireOp",EDGE,"E14.top"),sQuery(id+"F0.wireOp",EDGE,"E14.left")])]});
            var Q8;
            Q8=makeQuery(id+"F8.opExtrude","SWEPT_EDGE",EDGE,{"disambiguationData":[OSD([sQuery(id+"F0.wireOp",EDGE,"E15.bottom"),sQuery(id+"F0.wireOp",EDGE,"E15.right")])]});
            var Q9;
            Q9=makeQuery(id+"F8.opExtrude","SWEPT_EDGE",EDGE,{"disambiguationData":[OSD([sQuery(id+"F0.wireOp",EDGE,"E15.bottom"),sQuery(id+"F0.wireOp",EDGE,"E15.left")])]});
            var Q10;
            Q10=makeQuery(id+"F8.opExtrude","SWEPT_EDGE",EDGE,{"disambiguationData":[OSD([sQuery(id+"F0.wireOp",EDGE,"E9.top"),sQuery(id+"F0.wireOp",EDGE,"E9.left")])]});
            var Q11;
            Q11=makeQuery(id+"F8.opExtrude","SWEPT_EDGE",EDGE,{"disambiguationData":[OSD([sQuery(id+"F0.wireOp",EDGE,"E9.top"),sQuery(id+"F0.wireOp",EDGE,"E9.right")])]});
            var Q12;
            Q12=makeQuery(id+"F8.opExtrude","SWEPT_EDGE",EDGE,{"disambiguationData":[OSD([sQuery(id+"F0.wireOp",EDGE,"E11.bottom"),sQuery(id+"F0.wireOp",EDGE,"E11.left")])]});
            var Q13;
            Q13=makeQuery(id+"F8.opExtrude","SWEPT_EDGE",EDGE,{"disambiguationData":[OSD([sQuery(id+"F0.wireOp",EDGE,"E10.bottom"),sQuery(id+"F0.wireOp",EDGE,"E10.left")])]});
            var Q14;
            Q14=makeQuery(id+"F8.opExtrude","SWEPT_EDGE",EDGE,{"disambiguationData":[OSD([sQuery(id+"F0.wireOp",EDGE,"E10.top"),sQuery(id+"F0.wireOp",EDGE,"E10.left")])]});
            var Q15;
            Q15=makeQuery(id+"F8.opExtrude","SWEPT_EDGE",EDGE,{"disambiguationData":[OSD([sQuery(id+"F0.wireOp",EDGE,"E11.top"),sQuery(id+"F0.wireOp",EDGE,"E11.left")])]});
            fillet(context, id + "F24", {"entities" : qUnion([Q0, Q1, Q2, Q3, Q4, Q5, Q6, Q7, Q8, Q9, Q10, Q11, Q12, Q13, Q14, Q15]), "radius" : 0.7 * mm, "tangentPropagation" : true, "allowEdgeOverflow" : false});
        }
    });
